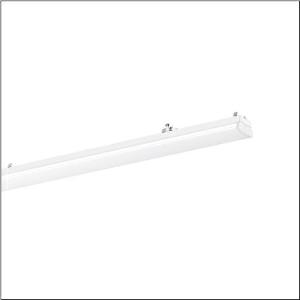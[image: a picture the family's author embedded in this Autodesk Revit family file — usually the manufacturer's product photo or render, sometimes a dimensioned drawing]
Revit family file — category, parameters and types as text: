
# Revit family: licross_r__21_recessed_opal_mo_52tl1ddv495g_d7bc
name_source: partatom
category: Lighting Fixtures
units: mm (PartAtom-declared; Revit-internal decimal feet)

## family parameters
Cut with Voids When Loaded = No
Host = Face
Light Source = No
Part Type = Normal
Room Calculation Point = No
Round Connector Dimension = Use Diameter
Shared = No

## types (1)
- --- (1 x LED, 9500 lm, 53.6 W, 4000K)
    Apparent Load = 54 VA
    CIE Flux Codes = 44 73 91 87 100
    Color Rendering = 80
    Color Temperature = 4000K
    Default Elevation = 1800 mm
    Description = Licross® 21 recessed opal MO, luminaire insert, of sheet steel, galvanised, coil coated, white, length: 2.250mm, width: 66mm, height: 67mm, LED rated luminous flux: 9.500lm, light colour: 840, control gear: DALI 2, with plug, 5-pole, with phase selection, mains connection: 220..240V, AC, 50/60Hz, rated input power: 54W, halogen-free wiring, primary optical cover: cover, of PMMA, light emission: direct with ceiling illumination distribution, primary light characteristic: symmetric, protection rating (complete): IP40, insulation class (complete): insulation class I (protective earthing), certification: CE, ENEC, VDE, UKCA, protection symbol: D if used in an environment without relevant dust loads with corresponding accessories, impact resistance: IK06, permissible ambient temperature for indoor applications: -25..+40°C, corresponds to IFS (International Featured Standards) requirements for safety and quality in the food industry, reducing of maximum allowable ambient temperature of 5°C with ceiling mounting, LABS conformity tested according to VDMA 24364:2018-05, packaging unit: 1 piece
    Height = 83 mm
    Lamp = 1 x LED
    Lamp Light Flux = 9500 lm
    Lamp Power = 53.6 W
    Lamp count = 1
    Length = 2250 mm
    Luminous efficacy = 177 lm/W
    Manufacturer = Siteco
    ModVariant = No
    Model = 52TL1DDV495G
    Mounting Place = Ceiling
    Mounting Type = Pendant
    Number of Poles = 1
    OnlyDefault = Yes
    Power Factor = 1
    Product Name = Licross® 21 recessed opal MO
    Product group = luminaire insert
    ProductGroupID = 901
    Protection Class = Protection class I
    Protection Degree = IP 40
    RLX_Detail_Level = 1
    RLX_Emergency_Light_Flux = 0 lm
    RLX_Emergency_Type = 0
    RLX_Emergency_Type_DB = No
    RlxData = <blob elided: 26469 chars, md5=4d7c1b17>
    Socket = socket
    Standby Power = 0 W
    System Light Flux = 9500 lm
    System Power = 54 W
    Type Comments = factory setting: luminous flux: 100 % | dim-lin: 254 | 246 mA
    Type Image = l_1313666.jpg
    URL = http://relux.com
    VarID = @adj_023387
    Voltage = 0 V
    Weight = 0.00 kg
    Width = 76 mm

## geometry (parser evidence)
native form markers: Blend x4, Sweep x13
no freeform markers — native parametric forms only
